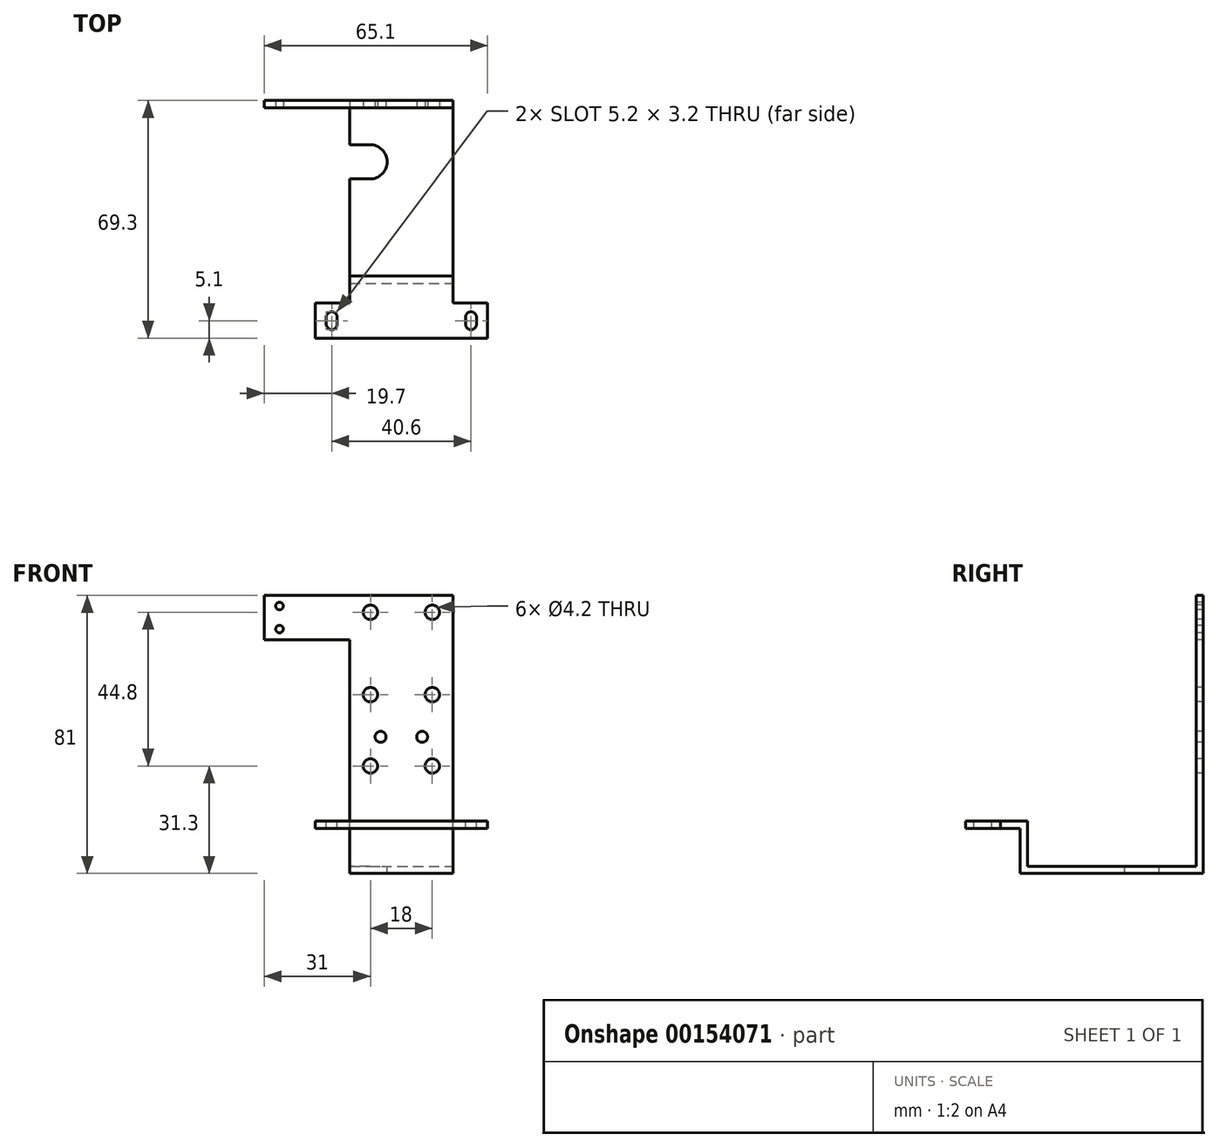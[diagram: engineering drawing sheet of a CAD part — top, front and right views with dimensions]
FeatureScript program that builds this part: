
annotation { "Feature Type Name" : "Feature", "Feature Type Description" : "" }
export const myFeature = defineFeature(function(context is Context, id is Id, definition is map)
    precondition{}
    {
        {
            var Q0;
            Q0=qCreatedBy(makeId("Front.planeOp"),FACE);
            var sketch = newSketch(context, id + "F0", { "sketchPlane" : qUnion([Q0])});
            skLineSegment(sketch, "E0.bottom", {"start": v(15, -40.5) * mm, "end": v(-15, -40.5) * mm});
            skLineSegment(sketch, "E0.top", {"start": v(15, 40.5) * mm, "end": v(-15, 40.5) * mm});
            skLineSegment(sketch, "E0.left", {"start": v(15, -40.5) * mm, "end": v(15, 40.5) * mm});
            skLineSegment(sketch, "E0.right", {"start": v(-15, -40.5) * mm, "end": v(-15, 40.5) * mm});
            skPoint(sketch, "E0.middle", {"position": v(0, 0) * mm});
            skSolve(sketch);
        }
        {
            var Q0;
            Q0=qSketchRegion(id+"F0",true);
            extrude(context, id + "F1", {"entities" : qUnion([Q0]), "depth" : 2.1 * mm});
        }
        {
            var Q0;
            Q0=makeQuery(id+"F1.opExtrude","CAP_FACE",FACE,{"disambiguationData":[OSD([sQuery(id+"F0.wireOp",EDGE,"E0.bottom"),sQuery(id+"F0.wireOp",EDGE,"E0.top"),sQuery(id+"F0.wireOp",EDGE,"E0.left"),sQuery(id+"F0.wireOp",EDGE,"E0.right")])],"isStart":false});
            var sketch = newSketch(context, id + "F2", { "sketchPlane" : qUnion([Q0])});
            skLineSegment(sketch, "E1.bottom", {"start": v(-15, -40.5) * mm, "end": v(15, -40.5) * mm});
            skLineSegment(sketch, "E1.top", {"start": v(-15, -38.4) * mm, "end": v(15, -38.4) * mm});
            skLineSegment(sketch, "E1.left", {"start": v(-15, -40.5) * mm, "end": v(-15, -38.4) * mm});
            skLineSegment(sketch, "E1.right", {"start": v(15, -40.5) * mm, "end": v(15, -38.4) * mm});
            skSolve(sketch);
        }
        {
            var Q0;
            Q0=qSketchRegion(id+"F2",true);
            extrude(context, id + "F3", {"entities" : qUnion([Q0]), "operationType" : NewBodyOperationType.ADD, "depth" : 51.2 * mm});
        }
        {
            var Q0;
            Q0=makeQuery(id+"F3.opExtrude","SWEPT_FACE",FACE,{"disambiguationData":[OSD([sQuery(id+"F2.wireOp",EDGE,"E1.top")])]});
            var sketch = newSketch(context, id + "F4", { "sketchPlane" : qUnion([Q0])});
            skLineSegment(sketch, "E2.bottom", {"start": v(-15, -53.3) * mm, "end": v(15, -53.3) * mm});
            skLineSegment(sketch, "E2.top", {"start": v(-15, -51.2) * mm, "end": v(15, -51.2) * mm});
            skLineSegment(sketch, "E2.left", {"start": v(-15, -53.3) * mm, "end": v(-15, -51.2) * mm});
            skLineSegment(sketch, "E2.right", {"start": v(15, -53.3) * mm, "end": v(15, -51.2) * mm});
            skSolve(sketch);
        }
        {
            var Q0;
            Q0=qSketchRegion(id+"F4",true);
            extrude(context, id + "F5", {"entities" : qUnion([Q0]), "operationType" : NewBodyOperationType.ADD, "depth" : 13.1 * mm});
        }
        {
            var Q0;
            Q0=makeQuery(id+"F5.boolean.opBoolean","MERGE",FACE,{"derivedFrom":[makeQuery(id+"F3.opExtrude","CAP_FACE",FACE,{"disambiguationData":[OSD([sQuery(id+"F2.wireOp",EDGE,"E1.bottom"),sQuery(id+"F2.wireOp",EDGE,"E1.top"),sQuery(id+"F2.wireOp",EDGE,"E1.left"),sQuery(id+"F2.wireOp",EDGE,"E1.right")])],"isStart":false}),makeQuery(id+"F5.opExtrude","SWEPT_FACE",FACE,{"disambiguationData":[OSD([sQuery(id+"F4.wireOp",EDGE,"E2.bottom")])]})]});
            var sketch = newSketch(context, id + "F6", { "sketchPlane" : qUnion([Q0])});
            skLineSegment(sketch, "E3.bottom", {"start": v(-15, -25.3) * mm, "end": v(15, -25.3) * mm});
            skLineSegment(sketch, "E3.top", {"start": v(-15, -27.4) * mm, "end": v(15, -27.4) * mm});
            skLineSegment(sketch, "E3.left", {"start": v(-15, -25.3) * mm, "end": v(-15, -27.4) * mm});
            skLineSegment(sketch, "E3.right", {"start": v(15, -25.3) * mm, "end": v(15, -27.4) * mm});
            skSolve(sketch);
        }
        {
            var Q0;
            Q0=qSketchRegion(id+"F6",true);
            extrude(context, id + "F7", {"entities" : qUnion([Q0]), "operationType" : NewBodyOperationType.ADD, "depth" : 16 * mm});
        }
        {
            var Q0;
            Q0=makeQuery(id+"F7.boolean.opBoolean","MERGE",FACE,{"derivedFrom":[makeQuery(id+"F5.opExtrude","CAP_FACE",FACE,{"disambiguationData":[OSD([sQuery(id+"F4.wireOp",EDGE,"E2.bottom"),sQuery(id+"F4.wireOp",EDGE,"E2.top"),sQuery(id+"F4.wireOp",EDGE,"E2.left"),sQuery(id+"F4.wireOp",EDGE,"E2.right")])],"isStart":false}),makeQuery(id+"F7.opExtrude","SWEPT_FACE",FACE,{"disambiguationData":[OSD([sQuery(id+"F6.wireOp",EDGE,"E3.bottom")])]})]});
            var sketch = newSketch(context, id + "F8", { "sketchPlane" : qUnion([Q0])});
            skLineSegment(sketch, "E4.bottom", {"start": v(-25.1, -69.3) * mm, "end": v(25.1, -69.3) * mm});
            skLineSegment(sketch, "E4.top", {"start": v(-25.1, -59.1) * mm, "end": v(25.1, -59.1) * mm});
            skLineSegment(sketch, "E4.left", {"start": v(-25.1, -69.3) * mm, "end": v(-25.1, -59.1) * mm});
            skLineSegment(sketch, "E4.right", {"start": v(25.1, -69.3) * mm, "end": v(25.1, -59.1) * mm});
            skLineSegment(sketch, "E5", {"start": v(0, -51.2) * mm, "end": v(0, -65.26) * mm});
            skSolve(sketch);
        }
        {
            var Q0;
            {var subQ3=sQuery(id+"F8.wireOp",EDGE,"E4.left");Q0=makeQuery(id+"F8.imprint","IMPRINT",FACE,{"disambiguationData":[TD([[makeQuery(id+"F8.imprint","IMPRINT",EDGE,{"derivedFrom":subQ3}),-1.0]])]});}
            var Q1;
            {var subQ3=sQuery(id+"F8.wireOp",EDGE,"E4.right");Q1=makeQuery(id+"F8.imprint","IMPRINT",FACE,{"disambiguationData":[TD([[makeQuery(id+"F8.imprint","IMPRINT",EDGE,{"derivedFrom":subQ3}),1.0]])]});}
            extrude(context, id + "F9", {"entities" : qUnion([Q0, Q1]), "operationType" : NewBodyOperationType.ADD, "oppositeDirection" : true, "depth" : 2.1 * mm});
        }
        {
            var Q0;
            {var subQ0=sQuery(id+"F8.wireOp",EDGE,"E4.top");var subQ1=sQuery(id+"F8.wireOp",EDGE,"E4.bottom");var subQ2=sQuery(id+"F6.wireOp",EDGE,"E3.bottom");var subQ3=sQuery(id+"F4.wireOp",EDGE,"E2.right");var subQ4=sQuery(id+"F4.wireOp",EDGE,"E2.left");Q0=makeQuery(id+"F9.boolean.opBoolean","MERGE",FACE,{"derivedFrom":[makeQuery(id+"F7.boolean.opBoolean","MERGE",FACE,{"derivedFrom":[makeQuery(id+"F5.opExtrude","CAP_FACE",FACE,{"disambiguationData":[OSD([sQuery(id+"F4.wireOp",EDGE,"E2.bottom"),sQuery(id+"F4.wireOp",EDGE,"E2.top"),subQ4,subQ3])],"isStart":false}),makeQuery(id+"F7.opExtrude","SWEPT_FACE",FACE,{"disambiguationData":[OSD([subQ2])]})]}),makeQuery(id+"F9.opExtrude","CAP_FACE",FACE,{"disambiguationData":[OSD([subQ4,subQ2,sQuery(id+"F6.wireOp",EDGE,"E3.left"),subQ1,subQ0,sQuery(id+"F8.wireOp",EDGE,"E4.left")])],"isStart":true}),makeQuery(id+"F9.opExtrude","CAP_FACE",FACE,{"disambiguationData":[OSD([subQ3,subQ2,sQuery(id+"F6.wireOp",EDGE,"E3.right"),subQ1,subQ0,sQuery(id+"F8.wireOp",EDGE,"E4.right")])],"isStart":true})]});}
            var sketch = newSketch(context, id + "F10", { "sketchPlane" : qUnion([Q0])});
            skArc(sketch, "E6", {"start": v(-21.9, -65.2) * mm, "mid": v(-20.3, -66.8) * mm, "end": v(-18.7, -65.2) * mm});
            skArc(sketch, "E7", {"start": v(-18.7, -63.2) * mm, "mid": v(-20.3, -61.6) * mm, "end": v(-21.9, -63.2) * mm});
            skLineSegment(sketch, "E8", {"start": v(-21.9, -63.2) * mm, "end": v(-21.9, -65.2) * mm});
            skLineSegment(sketch, "E9", {"start": v(-18.7, -65.2) * mm, "end": v(-18.7, -63.2) * mm});
            skLineSegment(sketch, "E10", {"start": v(-20.3, -63.2) * mm, "end": v(-20.3, -65.2) * mm});
            skPoint(sketch, "E11", {"position": v(-20.3, -64.2) * mm});
            skLineSegment(sketch, "E12", {"start": v(0, -69.3) * mm, "end": v(0, -51.2) * mm});
            skLineSegment(sketch, "E13.MirrorCS", {"start": v(18.7, -65.2) * mm, "end": v(18.7, -63.2) * mm});
            skArc(sketch, "E14.MirrorCS", {"start": v(18.7, -63.2) * mm, "mid": v(20.3, -61.6) * mm, "end": v(21.9, -63.2) * mm});
            skLineSegment(sketch, "E15.MirrorCS", {"start": v(21.9, -63.2) * mm, "end": v(21.9, -65.2) * mm});
            skArc(sketch, "E16.MirrorCS", {"start": v(21.9, -65.2) * mm, "mid": v(20.3, -66.8) * mm, "end": v(18.7, -65.2) * mm});
            skSolve(sketch);
        }
        {
            var Q0;
            Q0=makeQuery(id+"F10.imprint","IMPRINT",FACE,{"disambiguationData":[TD([[makeQuery(id+"F10.imprint","IMPRINT",EDGE,{"derivedFrom":sQuery(id+"F10.wireOp",EDGE,"E6")}),1.0]])]});
            var Q1;
            Q1=makeQuery(id+"F10.imprint","IMPRINT",FACE,{"disambiguationData":[TD([[makeQuery(id+"F10.imprint","IMPRINT",EDGE,{"derivedFrom":sQuery(id+"F10.wireOp",EDGE,"E13.MirrorCS")}),-1.0]])]});
            extrude(context, id + "F11", {"entities" : qUnion([Q0, Q1]), "operationType" : NewBodyOperationType.REMOVE, "endBound" : BoundingType.THROUGH_ALL, "oppositeDirection" : true, "depth" : 25 * mm});
        }
        {
            var Q0;
            Q0=makeQuery(id+"F3.opExtrude","SWEPT_FACE",FACE,{"disambiguationData":[OSD([sQuery(id+"F2.wireOp",EDGE,"E1.top")])]});
            var sketch = newSketch(context, id + "F12", { "sketchPlane" : qUnion([Q0])});
            skArc(sketch, "E17", {"start": v(-9.15, -22.9) * mm, "mid": v(-4.15, -17.9) * mm, "end": v(-9.15, -12.9) * mm});
            skLineSegment(sketch, "E18", {"start": v(-9.15, -12.9) * mm, "end": v(-15, -12.9) * mm});
            skLineSegment(sketch, "E19", {"start": v(-9.15, -22.9) * mm, "end": v(-15, -22.9) * mm});
            skLineSegment(sketch, "E20", {"start": v(-15, -22.9) * mm, "end": v(-15, -12.9) * mm});
            skSolve(sketch);
        }
        {
            var Q0;
            Q0=qSketchRegion(id+"F12",true);
            extrude(context, id + "F13", {"entities" : qUnion([Q0]), "operationType" : NewBodyOperationType.REMOVE, "endBound" : BoundingType.THROUGH_ALL, "oppositeDirection" : true, "depth" : 25 * mm});
        }
        {
            var Q0;
            Q0=makeQuery(id+"F1.opExtrude","CAP_FACE",FACE,{"disambiguationData":[OSD([sQuery(id+"F0.wireOp",EDGE,"E0.bottom"),sQuery(id+"F0.wireOp",EDGE,"E0.top"),sQuery(id+"F0.wireOp",EDGE,"E0.left"),sQuery(id+"F0.wireOp",EDGE,"E0.right")])],"isStart":false});
            var sketch = newSketch(context, id + "F14", { "sketchPlane" : qUnion([Q0])});
            skCircle(sketch, "E21", {"center": v(9, 35.6) * mm, "radius": 2.1 * mm});
            skCircle(sketch, "E22.0.1.0", {"center": v(9, 11.6) * mm, "radius": 2.1 * mm});
            skCircle(sketch, "E22.1.0.0", {"center": v(-9, 35.6) * mm, "radius": 2.1 * mm});
            skCircle(sketch, "E22.1.1.0", {"center": v(-9, 11.6) * mm, "radius": 2.1 * mm});
            skLineSegment(sketch, "E22.direction1", {"start": v(9, 35.6) * mm, "end": v(-9, 35.6) * mm, "construction": true});
            skLineSegment(sketch, "E22.direction2", {"start": v(9, 35.6) * mm, "end": v(9, 11.6) * mm, "construction": true});
            skCircle(sketch, "E23", {"center": v(9, -9.2) * mm, "radius": 2.1 * mm});
            skCircle(sketch, "E24.1.0.0", {"center": v(-9, -9.2) * mm, "radius": 2.1 * mm});
            skLineSegment(sketch, "E24.direction1", {"start": v(9, -9.2) * mm, "end": v(-9, -9.2) * mm, "construction": true});
            skCircle(sketch, "E25", {"center": v(6.05, -0.7) * mm, "radius": 1.6 * mm});
            skCircle(sketch, "E26", {"center": v(-6.05, -0.7) * mm, "radius": 1.6 * mm});
            skSolve(sketch);
        }
        {
            var Q0;
            Q0=qSketchRegion(id+"F14",true);
            extrude(context, id + "F15", {"entities" : qUnion([Q0]), "operationType" : NewBodyOperationType.REMOVE, "endBound" : BoundingType.THROUGH_ALL, "oppositeDirection" : true, "depth" : 25 * mm});
        }
        {
            var Q0;
            {var subQ0=sQuery(id+"F0.wireOp",EDGE,"E0.top");var subQ1=sQuery(id+"F0.wireOp",EDGE,"E0.right");Q0=makeQuery(id+"F13.boolean.opBoolean","SPLIT",FACE,{"disambiguationData":[TD([makeQuery(id+"F1.opExtrude","SWEPT_FACE",FACE,{"disambiguationData":[OSD([subQ0])]})])],"derivedFrom":makeQuery(id+"F7.boolean.opBoolean","MERGE",FACE,{"derivedFrom":[makeQuery(id+"F5.boolean.opBoolean","MERGE",FACE,{"derivedFrom":[makeQuery(id+"F3.boolean.opBoolean","MERGE",FACE,{"derivedFrom":[makeQuery(id+"F1.opExtrude","SWEPT_FACE",FACE,{"disambiguationData":[OSD([subQ1])]}),makeQuery(id+"F3.opExtrude","SWEPT_FACE",FACE,{"disambiguationData":[OSD([sQuery(id+"F2.wireOp",EDGE,"E1.left")])]})]}),makeQuery(id+"F5.opExtrude","SWEPT_FACE",FACE,{"disambiguationData":[OSD([sQuery(id+"F4.wireOp",EDGE,"E2.left")])]})]}),makeQuery(id+"F7.opExtrude","SWEPT_FACE",FACE,{"disambiguationData":[OSD([sQuery(id+"F6.wireOp",EDGE,"E3.left")])]})]})});}
            var sketch = newSketch(context, id + "F16", { "sketchPlane" : qUnion([Q0])});
            skLineSegment(sketch, "E27.bottom", {"start": v(0, 40.5) * mm, "end": v(2.1, 40.5) * mm});
            skLineSegment(sketch, "E27.top", {"start": v(0, 27.65) * mm, "end": v(2.1, 27.65) * mm});
            skLineSegment(sketch, "E27.left", {"start": v(0, 40.5) * mm, "end": v(0, 27.65) * mm});
            skLineSegment(sketch, "E27.right", {"start": v(2.1, 40.5) * mm, "end": v(2.1, 27.65) * mm});
            skSolve(sketch);
        }
        {
            var Q0;
            Q0 = qSketchRegion(id + "F16", true);
            extrude(context, id + "F17", {"entities" : qUnion([Q0]), "operationType" : NewBodyOperationType.ADD, "depth" : 25 * mm, "offsetDistance" : 25 * mm});
        }
        {
            var Q0;
            Q0=makeQuery(id+"F17.boolean.opBoolean","MERGE",FACE,{"derivedFrom":[makeQuery(id+"F1.opExtrude","CAP_FACE",FACE,{"disambiguationData":[OSD([sQuery(id+"F0.wireOp",EDGE,"E0.bottom"),sQuery(id+"F0.wireOp",EDGE,"E0.top"),sQuery(id+"F0.wireOp",EDGE,"E0.left"),sQuery(id+"F0.wireOp",EDGE,"E0.right")])],"isStart":false}),makeQuery(id+"F17.opExtrude","SWEPT_FACE",FACE,{"disambiguationData":[OSD([sQuery(id+"F16.wireOp",EDGE,"E27.right")])]})]});
            var sketch = newSketch(context, id + "F18", { "sketchPlane" : qUnion([Q0])});
            skCircle(sketch, "E28", {"center": v(-35.5, 37.42) * mm, "radius": 1.1 * mm});
            skCircle(sketch, "E29", {"center": v(-35.5, 30.72) * mm, "radius": 1.1 * mm});
            skLineSegment(sketch, "E30", {"start": v(-40, 34.08) * mm, "end": v(-26.44, 34.08) * mm});
            skSolve(sketch);
        }
        {
            var Q0;
            Q0=makeQuery(id+"F18.imprint","IMPRINT",FACE,{"disambiguationData":[TD([[makeQuery(id+"F18.imprint","IMPRINT",EDGE,{"derivedFrom":sQuery(id+"F18.wireOp",EDGE,"E28")}),1.0]])]});
            var Q1;
            Q1=makeQuery(id+"F18.imprint","IMPRINT",FACE,{"disambiguationData":[TD([[makeQuery(id+"F18.imprint","IMPRINT",EDGE,{"derivedFrom":sQuery(id+"F18.wireOp",EDGE,"E29")}),1.0]])]});
            extrude(context, id + "F19", {"entities" : qUnion([Q0, Q1]), "operationType" : NewBodyOperationType.REMOVE, "oppositeDirection" : true, "depth" : 25 * mm, "offsetDistance" : 25 * mm});
        }
    });
